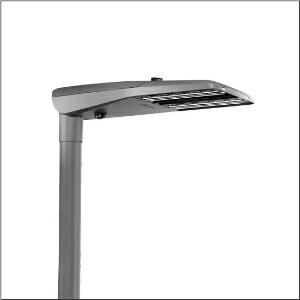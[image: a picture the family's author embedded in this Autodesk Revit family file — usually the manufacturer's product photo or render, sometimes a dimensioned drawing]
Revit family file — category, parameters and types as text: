
# Revit family: streetlight_sl_11_iq_midi___pc-r_5xc3f51y08me_63e7
name_source: partatom
category: Lighting Fixtures
units: mm (PartAtom-declared; Revit-internal decimal feet)

## family parameters
Cut with Voids When Loaded = No
Host = Face
Light Source = No
Part Type = Normal
Room Calculation Point = No
Round Connector Dimension = Use Diameter
Shared = No

## types (1)
- --- (1 x LED, 15540 lm, 122.7 W, 3000K)
    Apparent Load = 123 VA
    CIE Flux Codes = 37 73 96 100 100
    Color Rendering = 70
    Color Temperature = 3000K
    Default Elevation = 1800 mm
    Description = Streetlight SL 11 iQ midi, mast luminaire, primary light control with 3 zone facetted reflector, of plastic, silver coated, highly specular, primary optical cover: cover, of PMMA, transparent, light distribution: PC-R, light emission: direct distribution, primary light characteristic: asymmetric, right, installation type: post-top, side-entry, LED, High Power LED, rated luminous flux: 15.540lm, luminous efficacy: 127lm/W, light colour: 730, colour temperature: 3000K, control: presetting dimming logarithmic, Street-Remote, Auto-Match, Temp-Guard, Lumen-Switch, Night-Set, Smart-Wire, Light-Fading, Desk-Remote (wireless, voltage-free reading and setting of iQ features in the workshop via application-optimized NFC function/RFID function), optimised constant luminous flux control (CLO 2.0), with cable H07RN-F 5x 1.5mm², mains connection: 230..240V, AC, 50/60Hz, connection cable pre-assembled, cable length: 12,5m, start of lifetime: 123W, end of service life: 130W, reduction: 56W, luminaire housing, of diecast aluminium, powder-coated, Siteco® metallic grey (DB 702S), please order mast flange separately, inclination adjustable without tools: 0°, 5°, 10°, 15° (post-top) | 0°, -5°, -10°, -15° (side-entry), sealing non-destructively replaceable, multi-level sealing system, length: 780mm, width: 376mm, height: 118mm, mast flange for spigot size: 42mm (side-entry): 5XC10008XM4, 60/48mm (side-entry/post-top): 5XC10108XM2, 76/60mm (side-entry/post-top): 5XC10108XM1, equipment: Power, Smart Interface below and above, protection rating (complete): IP66, insulation class (complete): insulation class II (safety insulation), certification: CE, ENEC, VDE, UKCA, impact resistance: IK09, permissible operating ambient temperature for outdoor applications: -25..+50°C, standard-compliant lighting for roads and squares, Environmental Product Declaration (EPD) tested and certified by an independent institute, packaging unit: 1 piece

Light Distribution: PC-R
    Height = 118 mm
    Lamp = 1 x LED
    Lamp Light Flux = 15540 lm
    Lamp Power = 122.7 W
    Lamp count = 1
    Length = 780 mm
    Luminous efficacy = 127 lm/W
    Manufacturer = Siteco
    ModVariant = No
    Model = 5XC3F51Y08ME
    Number of Poles = 1
    OnlyDefault = Yes
    Power Factor = 1
    Product Name = Streetlight SL 11 iQ midi | PC-R
    Product group = mast luminaire | pylon top
    ProductGroupID = 6100
    Protection Class = Protection class II
    Protection Degree = IP 66
    RLX_Detail_Level = 1
    RLX_Emergency_Light_Flux = 0 lm
    RLX_Emergency_Type = 0
    RLX_Emergency_Type_DB = No
    RlxData = <blob elided: 73773 chars, md5=314de75d>
    Socket = socket
    Standby Power = 0 W
    System Light Flux = 15540 lm
    System Power = 123 W
    Type Comments = factory setting: luminous flux: 100 % | dim-lin: 254 | 552 mA
    Type Image = l_1004429.jpg
    URL = http://relux.com
    VarID = @adj_064257
    Voltage = 0 V
    Weight = 0.00 kg
    Width = 376 mm

## geometry (parser evidence)
native form markers: Blend x4, Sweep x10
no freeform markers — native parametric forms only
